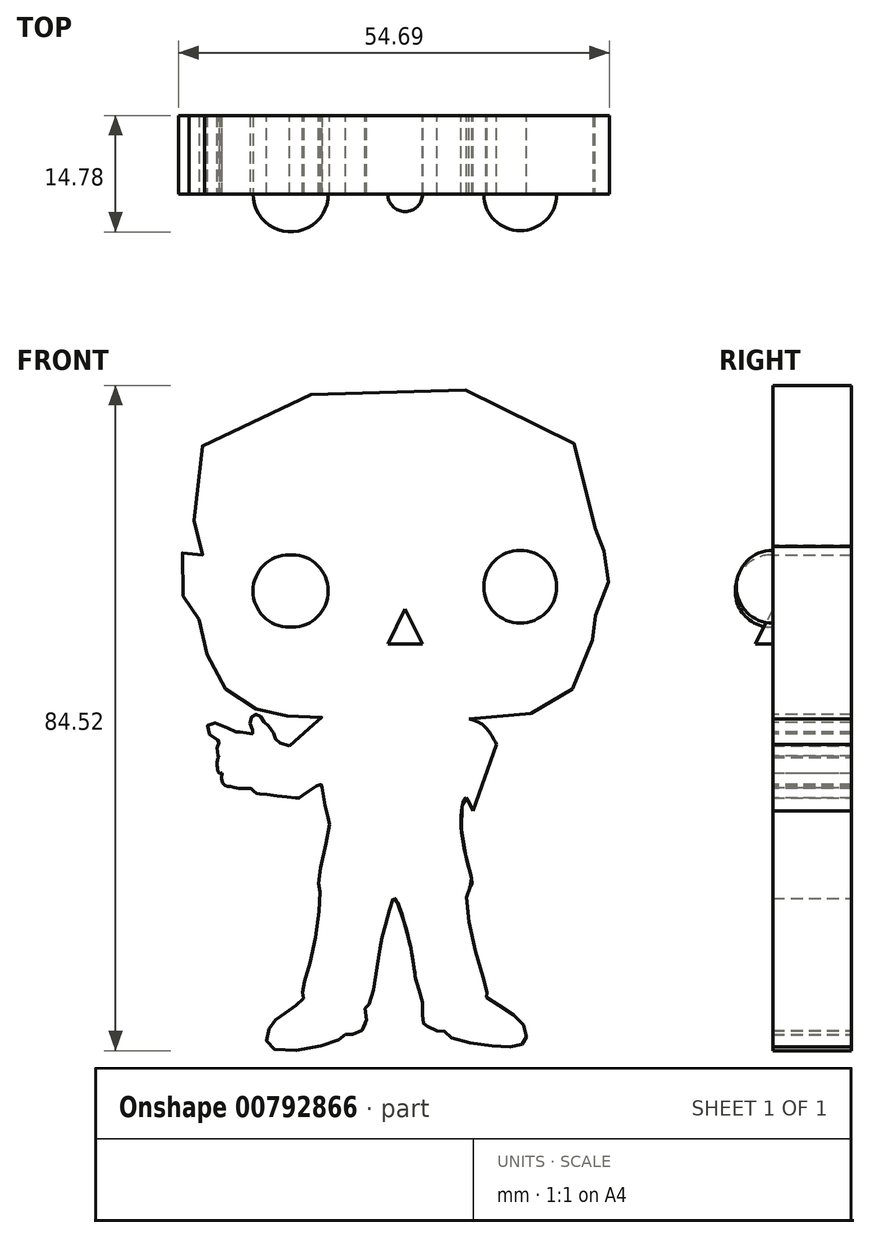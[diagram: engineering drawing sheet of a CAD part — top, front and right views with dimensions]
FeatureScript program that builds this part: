
annotation { "Feature Type Name" : "Feature", "Feature Type Description" : "" }
export const myFeature = defineFeature(function(context is Context, id is Id, definition is map)
    precondition{}
    {
        {
            var Q0;
            Q0=qCreatedBy(makeId("Front.planeOp"),FACE);
            var sketch = newSketch(context, id + "F0", { "sketchPlane" : qUnion([Q0])});
            skFitSpline(sketch, "E0", {"points": [v(22.22, -11.01) * mm, v(22.99, -14.9) * mm, v(23.17, -15.61) * mm, v(21.79, -22.85) * mm, v(21.98, -24.1) * mm, v(20.76, -33.2) * mm, v(19.78, -37.08) * mm, v(19.92, -37.65) * mm, v(18.86, -38.81) * mm, v(16.6, -40.34) * mm, v(15.37, -42.06) * mm, v(15.67, -44.1) * mm, v(23.67, -43.42) * mm, v(25.19, -42.4) * mm], "startDerivative": vector(8.88, -55.62) * mm, "endDerivative": vector(14.91, 16.52) * mm});
            skFitSpline(sketch, "E1", {"points": [v(25.19, -42.4) * mm, v(26.19, -42.4) * mm, v(27.82, -41.2) * mm, v(27.74, -38.96) * mm, v(28.18, -38.62) * mm, v(29.5, -31.8) * mm, v(30.06, -29.36) * mm, v(31.1, -25.56) * mm, v(31.48, -25.14) * mm, v(33.64, -32.11) * mm, v(34.27, -36) * mm, v(35.05, -38.81) * mm, v(35.04, -40.9) * mm, v(35.52, -41.29) * mm, v(36.85, -41.96) * mm], "startDerivative": vector(18.02, -2.53) * mm, "endDerivative": vector(66.42, -25.02) * mm});
            skFitSpline(sketch, "E2", {"points": [v(36.85, -41.96) * mm, v(37.7, -41.96) * mm, v(38.4, -42.67) * mm, v(43.81, -43.85) * mm, v(47.3, -43.82) * mm, v(48.1, -43.13) * mm, v(47.78, -41.17) * mm, v(45.27, -39.1) * mm, v(43.03, -37.52) * mm, v(43.16, -37.3) * mm, v(41.94, -32.6) * mm, v(40.7, -24.05) * mm, v(41.22, -23.49) * mm, v(40.05, -17.54) * mm, v(40.49, -12.38) * mm, v(41.57, -15.03) * mm, v(41.8, -19.22) * mm, v(42.44, -19.21) * mm, v(42.53, -20.13) * mm, v(41.8, -23) * mm, v(42.15, -24.04) * mm, v(43.36, -23.4) * mm, v(44.06, -22.48) * mm, v(44.5, -23.39) * mm, v(44.14, -26.15) * mm, v(44.36, -27.54) * mm, v(44.85, -27.68) * mm], "startDerivative": vector(40.7, 7.1) * mm, "endDerivative": vector(30.87, 39.74) * mm});
            skFitSpline(sketch, "E3", {"points": [v(44.85, -27.68) * mm, v(45.08, -27.85) * mm, v(45.49, -27.92) * mm, v(47.05, -25) * mm, v(47.35, -23.02) * mm, v(47.58, -21.77) * mm, v(47.3, -19.43) * mm, v(47.42, -18.58) * mm, v(47.8, -18.37) * mm, v(46.53, -11.5) * mm, v(42.82, -3.25) * mm, v(40.92, -2.33) * mm, v(40.28, -2.12) * mm], "startDerivative": vector(6.42, -5.12) * mm, "endDerivative": vector(-11.32, 3.97) * mm});
            skFitSpline(sketch, "E4", {"points": [v(22.22, -11.01) * mm, v(22.06, -10.67) * mm, v(19.52, -12.24) * mm, v(19.1, -12.39) * mm, v(14.63, -11.9) * mm, v(13.76, -11.71) * mm, v(13.24, -11.2) * mm, v(12.86, -11.16) * mm, v(11.46, -11.13) * mm, v(10.6, -10.88) * mm, v(10.12, -10.88) * mm, v(9.64, -10.53) * mm, v(9.5, -9.17) * mm], "startDerivative": vector(-0.31, 9.97) * mm, "endDerivative": vector(0.49, 16.53) * mm});
            skFitSpline(sketch, "E5", {"points": [v(9.5, -9.17) * mm, v(9.1, -9.17) * mm, v(9, -7.34) * mm, v(9.2, -7.22) * mm], "startDerivative": vector(-1.71, -0.78) * mm, "endDerivative": vector(1.15, 0.06) * mm});
            skFitSpline(sketch, "E6", {"points": [v(9.2, -7.22) * mm, v(9.2, -7.07) * mm, v(9, -7.04) * mm, v(8.99, -5.51) * mm, v(9.2, -5.3) * mm, v(9.2, -5.2) * mm, v(7.86, -4.14) * mm, v(8.02, -2.83) * mm, v(11.15, -3.96) * mm, v(11.5, -4.03) * mm, v(12.15, -3.98) * mm, v(13.2, -4.27) * mm, v(13.5, -4) * mm, v(13.2, -3.39) * mm, v(13.19, -2.21) * mm, v(13.73, -1.79) * mm, v(14.2, -1.85) * mm, v(14.82, -2.66) * mm, v(15.37, -3.14) * mm, v(16.22, -4.51) * mm, v(16.43, -5.1) * mm, v(18.08, -5.78) * mm], "startDerivative": vector(2.22, 9.65) * mm, "endDerivative": vector(30.05, -9) * mm});
            skFitSpline(sketch, "E7", {"points": [v(18.08, -5.78) * mm, v(18.95, -5.04) * mm, v(20.92, -3.27) * mm, v(21.82, -2.51) * mm, v(22.22, -2.22) * mm, v(22.22, -2.15) * mm, v(19, -2) * mm, v(16.37, -1.73) * mm, v(13.28, -0.8) * mm, v(10.16, 1.3) * mm, v(8.07, 4.66) * mm, v(6.72, 9.25) * mm, v(6.63, 10.45) * mm, v(6.62, 10.52) * mm, v(4.56, 13.36) * mm, v(4.45, 18.65) * mm, v(5.6, 19.69) * mm, v(7.2, 18.42) * mm, v(7.1, 19.57) * mm, v(7.2, 32.57) * mm, v(52.77, 34.41) * mm, v(57.14, 19.57) * mm, v(57.48, 19.57) * mm, v(58.4, 18.2) * mm, v(58.63, 15.32) * mm, v(57.37, 11.29) * mm, v(56.68, 10.48) * mm, v(56.8, 9.68) * mm, v(55.18, 3.35) * mm, v(50.7, -1.02) * mm, v(40.92, -2.33) * mm], "startDerivative": vector(38.98, 32.47) * mm, "endDerivative": vector(-190.6, -7) * mm});
            skSolve(sketch);
        }
        {
            var Q0;
            Q0 = qSketchRegion(id + "F0", true);
            extrude(context, id + "F1", {"entities" : qUnion([Q0]), "depth" : 10 * mm, "offsetDistance" : 25 * mm});
        }
        {
            var Q0;
            Q0=makeQuery(id+"F1.opExtrude","CAP_FACE",FACE,{"disambiguationData":[OSD([sQuery(id+"F0.wireOp",EDGE,"E0"),sQuery(id+"F0.wireOp",EDGE,"E1"),sQuery(id+"F0.wireOp",EDGE,"E2"),sQuery(id+"F0.wireOp",EDGE,"E3"),sQuery(id+"F0.wireOp",EDGE,"E4"),sQuery(id+"F0.wireOp",EDGE,"E5"),sQuery(id+"F0.wireOp",EDGE,"E6"),sQuery(id+"F0.wireOp",EDGE,"E7")])],"isStart":false});
            var sketch = newSketch(context, id + "F2", { "sketchPlane" : qUnion([Q0])});
            skArc(sketch, "E8", {"start": v(18.24, 18.5) * mm, "mid": v(13.46, 13.91) * mm, "end": v(18.24, 9.33) * mm});
            skLineSegment(sketch, "E9", {"start": v(18.24, 18.5) * mm, "end": v(18.24, 9.33) * mm});
            skSolve(sketch);
        }
        {
            var Q0;
            Q0=makeQuery(id+"F1.opExtrude","CAP_FACE",FACE,{"disambiguationData":[OSD([sQuery(id+"F0.wireOp",EDGE,"E0"),sQuery(id+"F0.wireOp",EDGE,"E1"),sQuery(id+"F0.wireOp",EDGE,"E2"),sQuery(id+"F0.wireOp",EDGE,"E3"),sQuery(id+"F0.wireOp",EDGE,"E4"),sQuery(id+"F0.wireOp",EDGE,"E5"),sQuery(id+"F0.wireOp",EDGE,"E6"),sQuery(id+"F0.wireOp",EDGE,"E7")])],"isStart":false});
            cPlane(context, id + "F3", {"entities" : qUnion([Q0]), "cplaneType" : CPlaneType.OFFSET, "offset" : 2 * mm, "oppositeDirection" : true, "width" : 150 * mm, "height" : 150 * mm});
        }
        {
            var Q0;
            Q0=makeQuery(id+"F1.opExtrude","CAP_FACE",FACE,{"disambiguationData":[OSD([sQuery(id+"F0.wireOp",EDGE,"E0"),sQuery(id+"F0.wireOp",EDGE,"E1"),sQuery(id+"F0.wireOp",EDGE,"E2"),sQuery(id+"F0.wireOp",EDGE,"E3"),sQuery(id+"F0.wireOp",EDGE,"E4"),sQuery(id+"F0.wireOp",EDGE,"E5"),sQuery(id+"F0.wireOp",EDGE,"E6"),sQuery(id+"F0.wireOp",EDGE,"E7")])],"isStart":false});
            var sketch = newSketch(context, id + "F4", { "sketchPlane" : qUnion([Q0])});
            skLineSegment(sketch, "E10", {"start": v(57.1, -5.3) * mm, "end": v(45.03, -3.72) * mm});
            skLineSegment(sketch, "E11", {"start": v(45.03, -3.72) * mm, "end": v(40.92, -15.43) * mm});
            skLineSegment(sketch, "E12", {"start": v(40.92, -15.43) * mm, "end": v(41.83, -27.68) * mm});
            skLineSegment(sketch, "E13", {"start": v(41.83, -27.68) * mm, "end": v(46.78, -34.16) * mm});
            skLineSegment(sketch, "E14", {"start": v(46.78, -34.16) * mm, "end": v(57.04, -10.73) * mm});
            skLineSegment(sketch, "E15", {"start": v(57.04, -10.73) * mm, "end": v(57.1, -5.3) * mm});
            skSolve(sketch);
        }
        {
            var Q0;
            Q0 = qSketchRegion(id + "F4", true);
            extrude(context, id + "F5", {"entities" : qUnion([Q0]), "operationType" : NewBodyOperationType.REMOVE, "oppositeDirection" : true, "depth" : 25 * mm, "offsetDistance" : 25 * mm});
        }
        {
            var Q0;
            Q0=makeQuery(id+"F1.opExtrude","CAP_FACE",FACE,{"disambiguationData":[OSD([sQuery(id+"F0.wireOp",EDGE,"E0"),sQuery(id+"F0.wireOp",EDGE,"E1"),sQuery(id+"F0.wireOp",EDGE,"E2"),sQuery(id+"F0.wireOp",EDGE,"E3"),sQuery(id+"F0.wireOp",EDGE,"E4"),sQuery(id+"F0.wireOp",EDGE,"E5"),sQuery(id+"F0.wireOp",EDGE,"E6"),sQuery(id+"F0.wireOp",EDGE,"E7")])],"isStart":false});
            var sketch = newSketch(context, id + "F6", { "sketchPlane" : qUnion([Q0])});
            skArc(sketch, "E16", {"start": v(47.4, 19.08) * mm, "mid": v(42.78, 14.46) * mm, "end": v(47.4, 9.83) * mm});
            skLineSegment(sketch, "E17", {"start": v(47.4, 19.08) * mm, "end": v(47.4, 9.83) * mm});
            skSolve(sketch);
        }
        {
            var Q0;
            Q0=makeQuery(id+"F6.imprint","IMPRINT",FACE,{"disambiguationData":[TD([[makeQuery(id+"F6.imprint","IMPRINT",EDGE,{"derivedFrom":sQuery(id+"F6.wireOp",EDGE,"E16")}),1.0]])]});
            var Q1;
            Q1=sQuery(id+"F6.wireOp",EDGE,"E17");
            revolve(context, id + "F7", {"operationType" : NewBodyOperationType.ADD, "surfaceOperationType" : NewSurfaceOperationType.NEW, "entities" : qUnion([Q0]), "axis" : qUnion([Q1]), "revolveType" : RevolveType.FULL});
        }
        {
            var Q0;
            Q0=makeQuery(id+"F2.imprint","IMPRINT",FACE,{"disambiguationData":[TD([[makeQuery(id+"F2.imprint","IMPRINT",EDGE,{"derivedFrom":sQuery(id+"F2.wireOp",EDGE,"E8")}),1.0]])]});
            var Q1;
            Q1=sQuery(id+"F2.wireOp",EDGE,"E9");
            revolve(context, id + "F8", {"operationType" : NewBodyOperationType.ADD, "surfaceOperationType" : NewSurfaceOperationType.NEW, "entities" : qUnion([Q0]), "axis" : qUnion([Q1]), "revolveType" : RevolveType.FULL});
        }
        {
            var Q0;
            Q0=makeQuery(id+"F1.opExtrude","CAP_FACE",FACE,{"disambiguationData":[OSD([sQuery(id+"F0.wireOp",EDGE,"E0"),sQuery(id+"F0.wireOp",EDGE,"E1"),sQuery(id+"F0.wireOp",EDGE,"E2"),sQuery(id+"F0.wireOp",EDGE,"E3"),sQuery(id+"F0.wireOp",EDGE,"E4"),sQuery(id+"F0.wireOp",EDGE,"E5"),sQuery(id+"F0.wireOp",EDGE,"E6"),sQuery(id+"F0.wireOp",EDGE,"E7")])],"isStart":false});
            var sketch = newSketch(context, id + "F9", { "sketchPlane" : qUnion([Q0])});
            skLineSegment(sketch, "E18", {"start": v(32.8, 11.6) * mm, "end": v(32.8, 7.18) * mm});
            skLineSegment(sketch, "E19", {"start": v(32.8, 7.18) * mm, "end": v(30.6, 7.18) * mm});
            skLineSegment(sketch, "E20", {"start": v(30.6, 7.18) * mm, "end": v(32.8, 11.6) * mm});
            skSolve(sketch);
        }
        {
            var Q0;
            Q0 = qSketchRegion(id + "F9", true);
            var Q1;
            Q1=sQuery(id+"F9.wireOp",EDGE,"E18");
            revolve(context, id + "F10", {"operationType" : NewBodyOperationType.ADD, "surfaceOperationType" : NewSurfaceOperationType.NEW, "entities" : qUnion([Q0]), "axis" : qUnion([Q1]), "revolveType" : RevolveType.FULL});
        }
        {
            var Q0;
            Q0=qCreatedBy(makeId("Front.planeOp"),FACE);
            var sketch = newSketch(context, id + "F11", { "sketchPlane" : qUnion([Q0])});
            skLineSegment(sketch, "E21", {"start": v(1.84, 19.37) * mm, "end": v(72.69, -22.92) * mm});
            skSolve(sketch);
        }
    });
